# Revit family: Bathtub-American_Standard-Studio-2973_Series
name_source: partatom
category: Plumbing Fixtures
revit_build: Autodesk Revit 2014 (Build: 20130308_1515(x64)
units: mm (PartAtom-declared; Revit-internal decimal feet)

## types (2) — shared parameters
ADA Compliant = Yes
Assembly Code = D2010510
CW Connection = Yes
CWFU = 3
Default Elevation = 0"
HW Connection = Yes
HWFU = 3
Height = 18"
Installation Type = Recess Installation
Length = 60"
Manufacturer = American Standard
Material = High Gloss Acrylic-American Standard-020-White
Price = Prices may vary. Please consult Manufacturer Representative for most up-to-date price list.
Product Documentation Link = https://www.americanstandard-us.com
Product Page URL = https://www.americanstandard-us.com
Shipping Weight = 60 lb
URL = https://www.americanstandard-us.com
Vent Connection = No
WFU = 4
Warranty Information = limited Lifetime Warranty
Waste Connection = Yes
Waste Connection Diameter = 2"
Waste Connection Radius = 1"
Width = 30"

## per-type parameters (varying)
| type | Connector Location | Description | Tub Geometry |
| 2973.202 | 9 3/4" | Studio 60" x 30" Bathing Pool with Built-In Apron and Left Side Drain | Bathtub-American_Standard-Studio-2973.202 : 2973.202 |
| 2973.102 | 50 1/4" | Studio 60" x 30" Bathing Pool with Built-In Apron and Right Side Drain | Bathtub-American_Standard-Studio-2973.102 : 2973.102 |

note: column(s) folded — value = type name in every type: Model

## geometry (parser evidence)
native form markers: Sweep x8
no freeform markers — native parametric forms only
